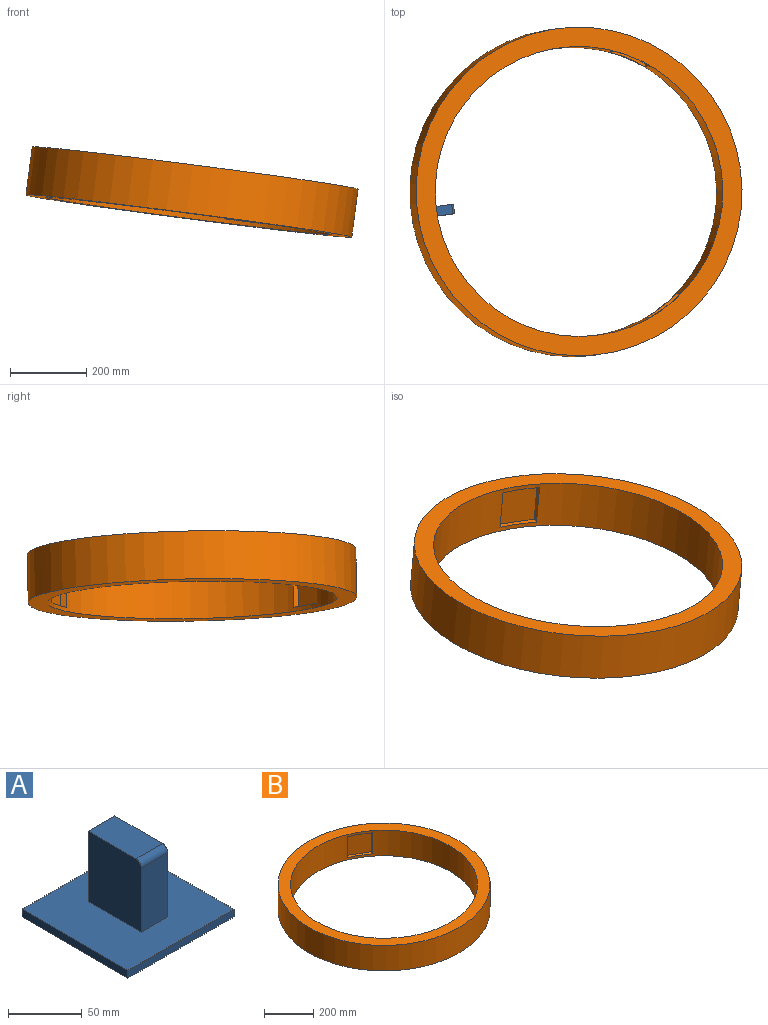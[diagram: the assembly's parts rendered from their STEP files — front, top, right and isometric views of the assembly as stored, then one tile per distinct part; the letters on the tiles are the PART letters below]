
ASSEMBLY  parts=2 mates=1
PART A: 12 faces, bbox 101.6x101.6x64.8 mm
  f0: plane 101.6x101.6mm, normal (0,0,1), area 9032.2mm2, adj f1,f2,f3,f4,f6,f7,f8,f9
  f1: plane 101.6x6.35mm, normal (0,-1,0), area 645.2mm2, adj f0,f2,f4,f5
  f2: plane 101.6x6.35mm, normal (1,0,0), area 645.2mm2, adj f0,f1,f3,f5
  f3: plane 101.6x6.35mm, normal (0,1,0), area 645.2mm2, adj f0,f2,f4,f5
  f4: plane 101.6x6.35mm, normal (-1,0,0), area 645.2mm2, adj f0,f1,f3,f5
  f5: plane 101.6x101.6mm, normal (0,0,-1), area 10322.6mm2, adj f1,f2,f3,f4
  f6: plane 53.34x25.4mm, normal (0,-1,0), area 1354.8mm2, adj f0,f7,f9,f11
  f7: plane 58.42x50.8mm, normal (1,0,0), area 2962.2mm2, adj f0,f6,f8,f10,f11
  f8: plane 58.42x25.4mm, normal (0,1,0), area 1483.9mm2, adj f0,f7,f9,f10
  f9: plane 58.42x50.8mm, normal (-1,0,0), area 2962.2mm2, adj f0,f6,f8,f10,f11
  f10: plane 45.72x25.4mm, normal (0,0,1), area 1161.3mm2, adj f7,f8,f9,f11
  f11: cylinder r=5.08mm len=25.4mm, axis (-1,0,0), area 202.7mm2, adj f6,f7,f9,f10
PART B: 19 faces, bbox 863.6x863.6x127 mm
  f0: cylinder r=381mm len=762mm, axis (0,0,-1), area 270986.4mm2, adj f2,f3,f4,f6,f7,f8,f9,f11
  f1: cylinder r=431.8mm len=863.6mm, axis (0,0,-1), area 344561.1mm2, adj f2,f3
  f2: plane 863.6x863.6mm, normal (0,0,1), area 129717.1mm2, adj f0,f1
  f3: plane 863.6x863.6mm, normal (0,0,-1), area 129717.1mm2, adj f0,f1
  f4: plane 104.78x16.32mm, normal (0,0,-1), area 1456.8mm2, adj f0,f5,f7,f8
  f5: plane 104.78x104.78mm, normal (1,0,0), area 10977.8mm2, adj f4,f6,f7,f8
  f6: plane 104.78x16.32mm, normal (0,0,1), area 1456.8mm2, adj f0,f5,f7,f8
  f7: plane 104.78x16.32mm, normal (0,-1,0), area 1709.8mm2, adj f0,f4,f5,f6
  f8: plane 104.78x16.32mm, normal (0,1,0), area 1709.8mm2, adj f0,f4,f5,f6
  f9: plane 98.9x66.52mm, normal (0,0,-1), area 1456.8mm2, adj f0,f10,f12,f13
  f10: plane 104.78x90.74mm, normal (-0.5,0.87,0), area 10977.8mm2, adj f9,f11,f12,f13
  f11: plane 98.9x66.52mm, normal (0,0,1), area 1456.8mm2, adj f0,f10,f12,f13
  f12: plane 104.78x14.13mm, normal (0.87,0.5,0), area 1709.8mm2, adj f0,f9,f10,f11
  f13: plane 104.78x14.13mm, normal (-0.87,-0.5,0), area 1709.8mm2, adj f0,f9,f10,f11
  f14: plane 98.9x66.52mm, normal (0,0,-1), area 1456.8mm2, adj f0,f15,f17,f18
  f15: plane 104.78x90.74mm, normal (-0.5,-0.87,0), area 10977.8mm2, adj f14,f16,f17,f18
  f16: plane 98.9x66.52mm, normal (0,0,1), area 1456.8mm2, adj f0,f15,f17,f18
  f17: plane 104.78x14.13mm, normal (-0.87,0.5,0), area 1709.8mm2, adj f0,f14,f15,f16
  f18: plane 104.78x14.13mm, normal (0.87,-0.5,0), area 1709.8mm2, adj f0,f14,f15,f16
PLACE A rot(axis=(-0.65,0.57,-0.5),120.3deg) t=(-14.74,34.12,46.92)mm
PLACE B rot(axis=(-0.05,0.68,0.73),10.9deg) t=(371.9,87.99,-4.12)mm
MATE fastened B.f5 <-> A.f5  axis (0.98,0.14,-0.13) through (-14.74,34.12,46.92)mm
